# Revit family: Lighting-Sconce-Waterworks-Flyte
name_source: partatom
category: Lighting Fixtures
revit_build: Autodesk Revit MEP 2014 (Build: 20140709_2115(x64)
units: mm (PartAtom-declared; Revit-internal decimal feet)

## types (3) — shared parameters
Apparent Load = 120 VA
Assembly Code = D5020200
Certification CUL = Yes
Certification UL = Yes
Code Compliance = UL and CUL
Color Filter = 16777215
Default Elevation = 2' - 10"
Depth = 0' - 5 5/8"
Dimming Lamp Color Temperature Shift = <None>
Height = 1' - 1"
Keynote = 22 40 00
Lamp = Candelabra E12
Length = 0' - 4"
Manufacturer = Waterworks
Model = FLLT01
Photometric Web File = generic
Product Documentation Link = http://assets.waterworks.com
Product Page URL = http://www.waterworks.com
Tilt Angle = 0.00°
URL = http://www.waterworks.com
Version = 2014 - v1.0a
Voltage = 120 V
Warranty = http://www.waterworks.com
Wattage Comments = 60 Watts
‌Installation Requirements or Notes = Uses E12 Candelabra/Torpedo bulb

## per-type parameters (varying)
| type | Constraint | Description | Finish | Model SKU | Product Name |
| Chrome | 1 | Wall Mounted Single Arm Sconce with Fabric Shade in Chrome | Metal - Waterworks - Chrome | 18-36828-03427 | Flyte Wall Mounted Single Arm Sconce with Fabric Shade in Chrome |
| Nickel | 2 | Wall Mounted Single Arm Sconce with Fabric Shade in Nickel | Metal - Waterworks - Nickel | 18-50139-43116 | Flyte Wall Mounted Single Arm Sconce with Fabric Shade in Nickel |
| Brass | 3 | Wall Mounted Single Arm Sconce with Fabric Shade in Unlacquered Brass | Metal - Waterworks - Unlacquered Brass | 18-46643-85088 | Flyte Wall Mounted Single Arm Sconce with Fabric Shade in Unlacquered Brass |

## geometry (parser evidence)
native form markers: Sweep x3
no freeform markers — native parametric forms only
